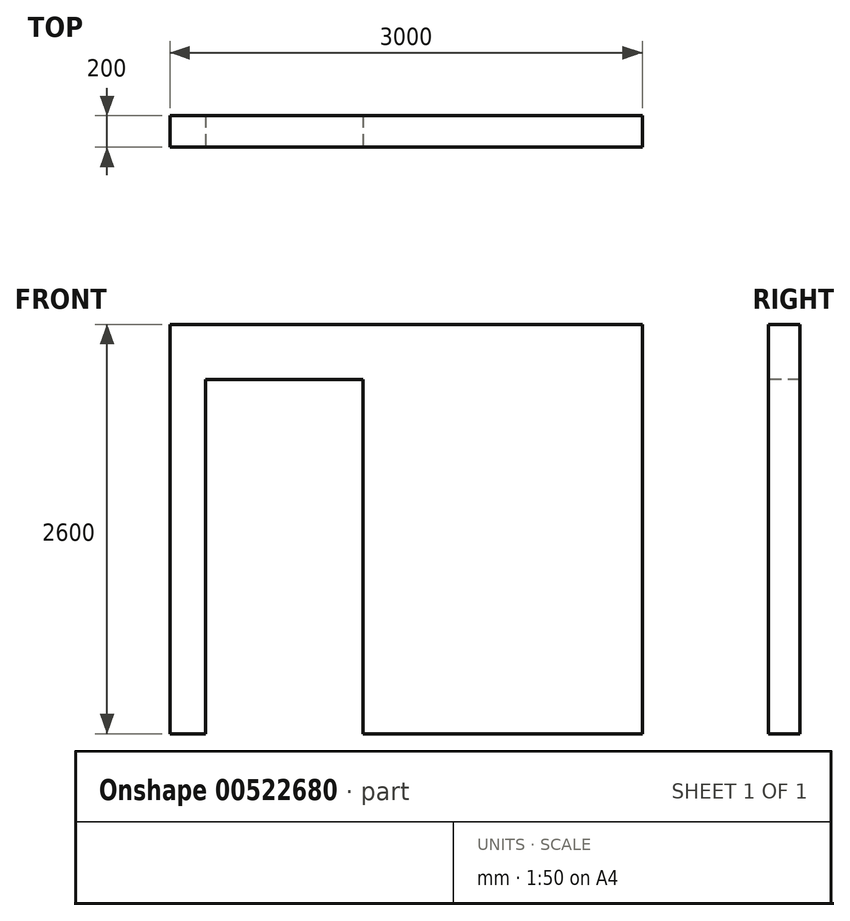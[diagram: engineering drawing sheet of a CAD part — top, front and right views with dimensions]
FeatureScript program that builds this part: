
annotation { "Feature Type Name" : "Feature", "Feature Type Description" : "" }
export const myFeature = defineFeature(function(context is Context, id is Id, definition is map)
    precondition{}
    {
        {
            var Q0;
            Q0=qCreatedBy(makeId("Front.planeOp"),FACE);
            var sketch = newSketch(context, id + "F0", { "sketchPlane" : qUnion([Q0])});
            skLineSegment(sketch, "E0.bottom", {"start": v(0, 0) * mm, "end": v(3000, 0) * mm});
            skLineSegment(sketch, "E0.top", {"start": v(0, 2600) * mm, "end": v(3000, 2600) * mm});
            skLineSegment(sketch, "E0.left", {"start": v(0, 0) * mm, "end": v(0, 2600) * mm});
            skLineSegment(sketch, "E0.right", {"start": v(3000, 0) * mm, "end": v(3000, 2600) * mm});
            skSolve(sketch);
        }
        {
            var Q0;
            Q0 = qSketchRegion(id + "F0", true);
            extrude(context, id + "F1", {"entities" : qUnion([Q0]), "depth" : 200 * mm, "offsetDistance" : 25 * mm});
        }
        {
            var Q0;
            Q0=makeQuery(id+"F1.opExtrude","CAP_FACE",FACE,{"disambiguationData":[OSD([sQuery(id+"F0.wireOp",EDGE,"E0.bottom"),sQuery(id+"F0.wireOp",EDGE,"E0.top"),sQuery(id+"F0.wireOp",EDGE,"E0.left"),sQuery(id+"F0.wireOp",EDGE,"E0.right")])],"isStart":false});
            var sketch = newSketch(context, id + "F2", { "sketchPlane" : qUnion([Q0])});
            skLineSegment(sketch, "E1.bottom", {"start": v(225, 0) * mm, "end": v(1225, 0) * mm});
            skLineSegment(sketch, "E1.top", {"start": v(225, 2250) * mm, "end": v(1225, 2250) * mm});
            skLineSegment(sketch, "E1.left", {"start": v(225, 0) * mm, "end": v(225, 2250) * mm});
            skLineSegment(sketch, "E1.right", {"start": v(1225, 0) * mm, "end": v(1225, 2250) * mm});
            skSolve(sketch);
        }
        {
            var Q0;
            Q0=makeQuery(id+"F2.imprint","IMPRINT",FACE,{"disambiguationData":[TD([[makeQuery(id+"F2.imprint","IMPRINT",EDGE,{"derivedFrom":sQuery(id+"F2.wireOp",EDGE,"E1.bottom")}),1.0]])]});
            extrude(context, id + "F3", {"entities" : qUnion([Q0]), "operationType" : NewBodyOperationType.REMOVE, "endBound" : BoundingType.THROUGH_ALL, "oppositeDirection" : true, "depth" : 25 * mm, "offsetDistance" : 25 * mm});
        }
    });
